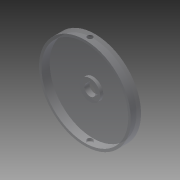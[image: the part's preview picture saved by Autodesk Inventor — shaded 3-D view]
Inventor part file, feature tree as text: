
AUTODESK INVENTOR PART (.ipt)
format: ipt  version: 2014 (Build 180170000, 170)  size: 128,000 bytes
history: native  units: mm
features: sketch x6, extrude x3, hole x3, plane x2
ambient origin geometry x8: Origin, YZ Plane, XZ Plane, XY Plane, X Axis, Y Axis, Z Axis, Center Point
bodies: Solid1 (feature_tree)
feature tree (14):
  extrude  "Extrusion1"  Depth=10.0mm TaperAngle=0.0deg
  extrude  "Extrusion2"  Depth=5.0mm TaperAngle=0.0deg
  extrude  "Extrusion3"  Depth=3.0mm TaperAngle=0.0deg
  hole  "Hole1"  [1 undecoded]
  plane  "Work Plane1"
  sketch  "Sketch5"  dims[d17=5.0mm d18=-45.0mm]
  plane  "Work Plane2"
  sketch  "Sketch6"  dims[d19=5.0mm d20=5.0mm d21=6.0mm d22=4.0mm d23=2.0mm d24=90.0deg d25=8.0mm d26=20.594885mm d27=5.0mm d28=6.0mm d29=4.0mm d30=2.0mm d31=90.0deg d32=8.0mm d33=20.594885mm]
  hole  "Hole2"  [1 undecoded]
  hole  "Hole3"  [1 undecoded]
  sketch  "Sketch1"  dims[d0=90.0mm d1=10.0mm d2=0.0mm]
  sketch  "Sketch2"  dims[d3=85.0mm d4=5.0mm d5=0.0mm]
  sketch  "Sketch3"  dims[d6=20.0mm d7=3.0mm d8=0.0mm]
  sketch  "Sketch4"  dims[d9=11.0mm d10=6.0mm d11=4.0mm d12=2.0mm d13=90.0deg d14=8.0mm d15=20.594885mm d16=45.0mm]
note: 3 required parameter values undecoded (feature->parameter linkage not recoverable at this tier; creation-order binding heuristic only, values carry confidence <= 0.55)
